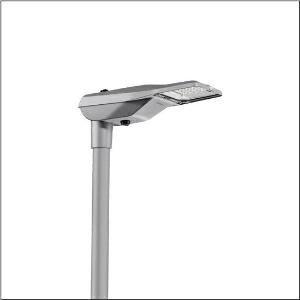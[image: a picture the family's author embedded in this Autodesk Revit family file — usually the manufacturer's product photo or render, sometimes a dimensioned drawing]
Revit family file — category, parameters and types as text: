
# Revit family: streetlight_sl_21_iq_micro___st1_0a_5xe1d31y08cb_1c09
name_source: partatom
category: Lighting Fixtures
units: mm (PartAtom-declared; Revit-internal decimal feet)

## family parameters
Cut with Voids When Loaded = No
Host = Face
Light Source = No
Part Type = Normal
Room Calculation Point = No
Round Connector Dimension = Use Diameter
Shared = No

## types (1)
- --- (1 x LED, 2880 lm, 19.1 W, 3000K)
    Apparent Load = 19 VA
    CIE Flux Codes = 37 72 97 100 100
    Color Rendering = 70
    Color Temperature = 3000K
    Default Elevation = 1800 mm
    Description = Streetlight SL 21 iQ micro, mast luminaire, primary light control with lens, of PMMA, primary optical cover: cover, of toughened safety glass, transparent, light distribution: ST1.0a, light emission: direct distribution, primary light characteristic: asymmetric, installation type: post-top, side-entry, LED, High Power LED, rated luminous flux: 2.880lm, luminous efficacy: 151lm/W, light colour: 730, colour temperature: 3000K, control: pre-setting: logarithmic dimming characteristic, Street-Remote, Auto-Match, Temp-Guard, Lumen-Switch, Night-Set, Smart-Wire, Light-Fading, Desk-Remote (wireless, voltage-free reading and setting of iQ features in the workshop via application-optimized NFC function/RFID function), optimised constant luminous flux control (CLO 2.0), mains connection: 220..240V, AC, 50/60Hz, start of lifetime: 19W, end of service life: 20W, reduction: 9W, luminaire housing, of diecast aluminium, powder-coated, Siteco® metallic grey (DB 702S), corrosivity category C5 mid according to DIN EN ISO 12944, please order mast flange separately, inclination adjustable: 0°, 5°, 10°, 15°, sealing non-destructively replaceable, multi-level sealing system, length: 528mm, width: 235mm, height: 110mm, mast flange for spigot size: 42mm (side-entry): 5XC10008XM4, 60/48mm (side-entry/post-top): 5XC10108XM2, 76/60mm (side-entry/post-top): 5XC10108XM1, Smart Interface below and above, protection rating (complete): IP66, insulation class (complete): insulation class II (safety insulation), certification: CE, ENEC, ENEC+, VDE, impact resistance: IK09, permissible operating ambient temperature for outdoor applications: -40..+50°C, standard-compliant lighting for roads and squares, packaging unit: 1 piece

Light Distribution: ST1.0a
    Height = 110 mm
    Lamp = 1 x LED
    Lamp Light Flux = 2880 lm
    Lamp Power = 19.1 W
    Lamp count = 1
    Length = 528 mm
    Luminous efficacy = 151 lm/W
    Manufacturer = Siteco
    ModVariant = No
    Model = 5XE1D31Y08CB
    Number of Poles = 1
    OnlyDefault = Yes
    Power Factor = 1
    Product Name = Streetlight SL 21 iQ micro | ST1.0a
    Product group = mast luminaire | pylon top
    ProductGroupID = 6100
    Protection Class = Protection class II
    Protection Degree = IP 66
    RLX_Detail_Level = 1
    RLX_Emergency_Light_Flux = 0 lm
    RLX_Emergency_Type = 0
    RLX_Emergency_Type_DB = No
    RlxData = <blob elided: 98529 chars, md5=e1dccb05>
    Socket = socket
    Standby Power = 0 W
    System Light Flux = 2880 lm
    System Power = 19 W
    Type Comments = factory setting: luminous flux: 100 % | dim-lin: 254 | 387 mA
    Type Image = l_1007239.jpg
    URL = http://relux.com
    VarID = @adj_084303
    Voltage = 0 V
    Weight = 0.00 kg
    Width = 235 mm

## geometry (parser evidence)
native form markers: Blend x4, Sweep x10
no freeform markers — native parametric forms only
